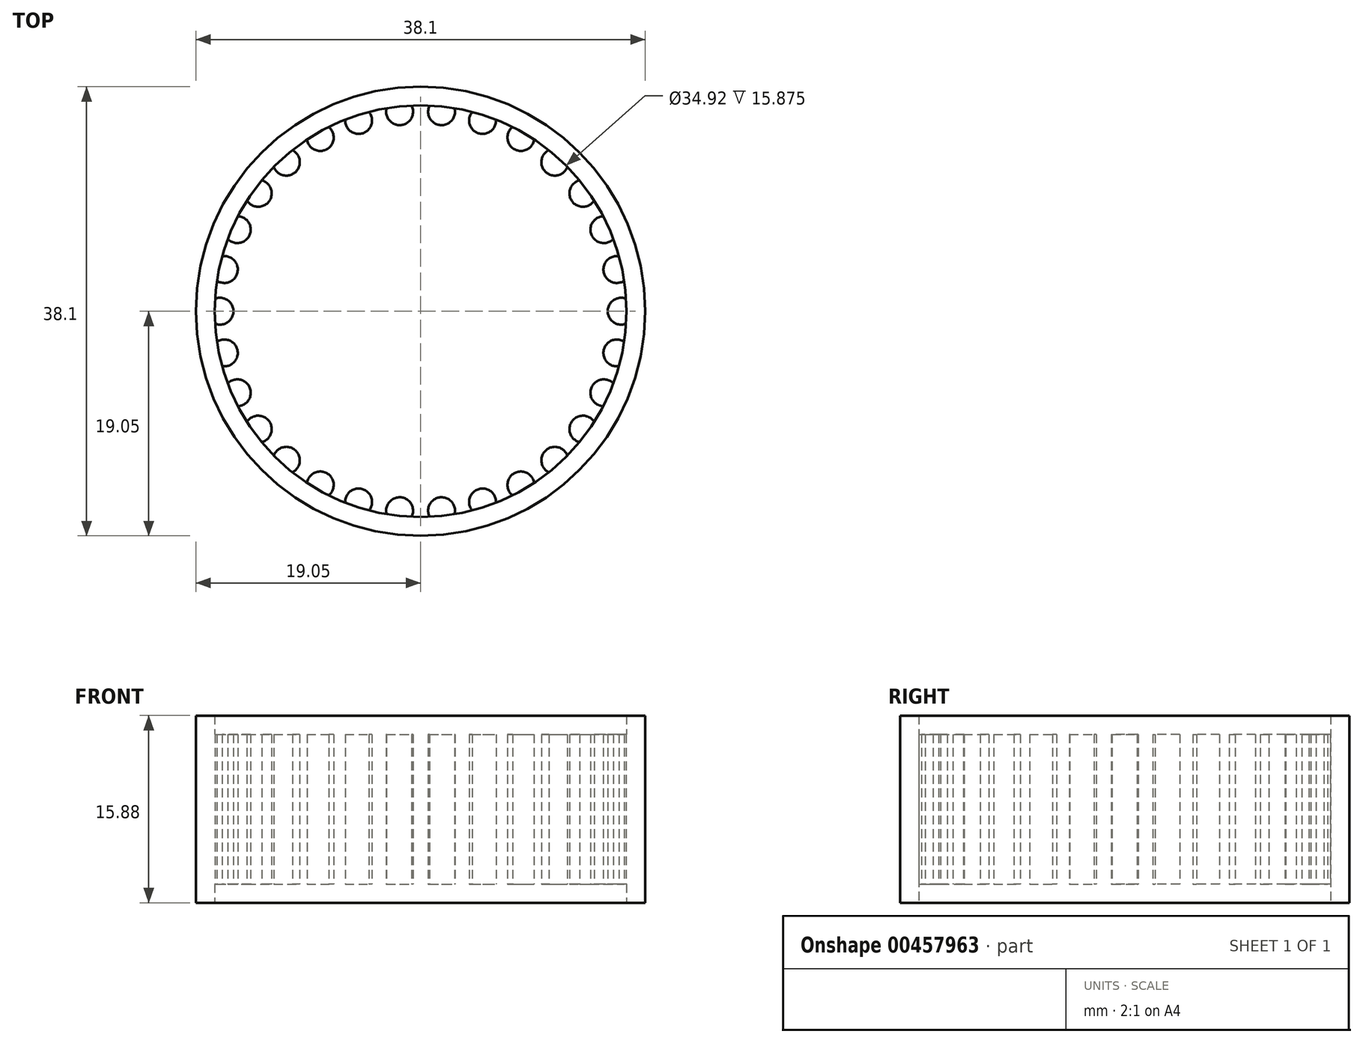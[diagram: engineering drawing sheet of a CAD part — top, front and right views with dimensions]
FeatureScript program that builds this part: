
annotation { "Feature Type Name" : "Feature", "Feature Type Description" : "" }
export const myFeature = defineFeature(function(context is Context, id is Id, definition is map)
    precondition{}
    {
        {
            var Q0;
            Q0=qCreatedBy(makeId("Front.planeOp"),FACE);
            var sketch = newSketch(context, id + "F0", { "sketchPlane" : qUnion([Q0])});
            skLineSegment(sketch, "E0.left", {"start": v(-19.05, 7.94) * mm, "end": v(-19.05, -7.94) * mm});
            skLineSegment(sketch, "E0.right", {"start": v(-17.46, 7.94) * mm, "end": v(-17.46, -7.94) * mm});
            skLineSegment(sketch, "E1", {"start": v(0, 0) * mm, "end": v(0, 72.18) * mm, "construction": true});
            skLineSegment(sketch, "E2", {"start": v(-19.05, 7.94) * mm, "end": v(-17.46, 7.94) * mm});
            skLineSegment(sketch, "E3", {"start": v(-17.46, -7.94) * mm, "end": v(-19.05, -7.94) * mm});
            skSolve(sketch);
        }
        {
            var Q0;
            Q0=makeQuery(id+"F0.imprint","IMPRINT",FACE,{"disambiguationData":[TD([[makeQuery(id+"F0.imprint","IMPRINT",EDGE,{"derivedFrom":sQuery(id+"F0.wireOp",EDGE,"E0.left")}),1.0]])]});
            var Q1;
            Q1=sQuery(id+"F0.wireOp",EDGE,"E1");
            revolve(context, id + "F1", {"entities" : qUnion([Q0]), "axis" : qUnion([Q1]), "revolveType" : RevolveType.FULL});
        }
        {
            var Q0;
            Q0=qCreatedBy(makeId("Top.planeOp"),FACE);
            var sketch = newSketch(context, id + "F2", { "sketchPlane" : qUnion([Q0])});
            skCircle(sketch, "E4", {"center": v(0, 0) * mm, "radius": 15.88 * mm, "construction": true});
            skCircle(sketch, "E5", {"center": v(0, 0) * mm, "radius": 18.15 * mm, "construction": true});
            skLineSegment(sketch, "E6", {"start": v(18.15, 0) * mm, "end": v(15.88, 0) * mm, "construction": true});
            skCircle(sketch, "E7", {"center": v(17.01, 0) * mm, "radius": 1.14 * mm});
            skCircle(sketch, "E8.1.0", {"center": v(16.64, 3.54) * mm, "radius": 1.14 * mm});
            skCircle(sketch, "E8.2.0", {"center": v(15.54, 6.92) * mm, "radius": 1.14 * mm});
            skCircle(sketch, "E8.3.0", {"center": v(13.77, 10) * mm, "radius": 1.14 * mm});
            skCircle(sketch, "E8.4.0", {"center": v(11.39, 12.64) * mm, "radius": 1.14 * mm});
            skCircle(sketch, "E8.5.0", {"center": v(8.5, 14.74) * mm, "radius": 1.14 * mm});
            skCircle(sketch, "E8.6.0", {"center": v(5.26, 16.18) * mm, "radius": 1.14 * mm});
            skCircle(sketch, "E8.7.0", {"center": v(1.78, 16.92) * mm, "radius": 1.14 * mm});
            skCircle(sketch, "E8.8.0", {"center": v(-1.78, 16.92) * mm, "radius": 1.14 * mm});
            skCircle(sketch, "E8.9.0", {"center": v(-5.26, 16.18) * mm, "radius": 1.14 * mm});
            skCircle(sketch, "E8.10.0", {"center": v(-8.5, 14.74) * mm, "radius": 1.14 * mm});
            skCircle(sketch, "E8.11.0", {"center": v(-11.39, 12.64) * mm, "radius": 1.14 * mm});
            skCircle(sketch, "E8.12.0", {"center": v(-13.77, 10) * mm, "radius": 1.14 * mm});
            skCircle(sketch, "E8.13.0", {"center": v(-15.54, 6.92) * mm, "radius": 1.14 * mm});
            skCircle(sketch, "E8.14.0", {"center": v(-16.64, 3.54) * mm, "radius": 1.14 * mm});
            skCircle(sketch, "E8.15.0", {"center": v(-17.01, 0) * mm, "radius": 1.14 * mm});
            skCircle(sketch, "E8.16.0", {"center": v(-16.64, -3.54) * mm, "radius": 1.14 * mm});
            skCircle(sketch, "E8.17.0", {"center": v(-15.54, -6.92) * mm, "radius": 1.14 * mm});
            skCircle(sketch, "E8.18.0", {"center": v(-13.77, -10) * mm, "radius": 1.14 * mm});
            skCircle(sketch, "E8.19.0", {"center": v(-11.39, -12.64) * mm, "radius": 1.14 * mm});
            skCircle(sketch, "E8.20.0", {"center": v(-8.5, -14.74) * mm, "radius": 1.14 * mm});
            skCircle(sketch, "E8.21.0", {"center": v(-5.26, -16.18) * mm, "radius": 1.14 * mm});
            skCircle(sketch, "E8.22.0", {"center": v(-1.78, -16.92) * mm, "radius": 1.14 * mm});
            skCircle(sketch, "E8.23.0", {"center": v(1.78, -16.92) * mm, "radius": 1.14 * mm});
            skCircle(sketch, "E8.24.0", {"center": v(5.26, -16.18) * mm, "radius": 1.14 * mm});
            skCircle(sketch, "E8.25.0", {"center": v(8.5, -14.74) * mm, "radius": 1.14 * mm});
            skCircle(sketch, "E8.26.0", {"center": v(11.39, -12.64) * mm, "radius": 1.14 * mm});
            skCircle(sketch, "E8.27.0", {"center": v(13.77, -10) * mm, "radius": 1.14 * mm});
            skCircle(sketch, "E8.28.0", {"center": v(15.54, -6.92) * mm, "radius": 1.14 * mm});
            skCircle(sketch, "E8.29.0", {"center": v(16.64, -3.54) * mm, "radius": 1.14 * mm});
            skSolve(sketch);
        }
        {
            var Q0;
            Q0 = qSketchRegion(id + "F2", true);
            extrude(context, id + "F3", {"entities" : qUnion([Q0]), "operationType" : NewBodyOperationType.ADD, "endBound" : BoundingType.SYMMETRIC, "depth" : 12.7 * mm});
        }
    });
